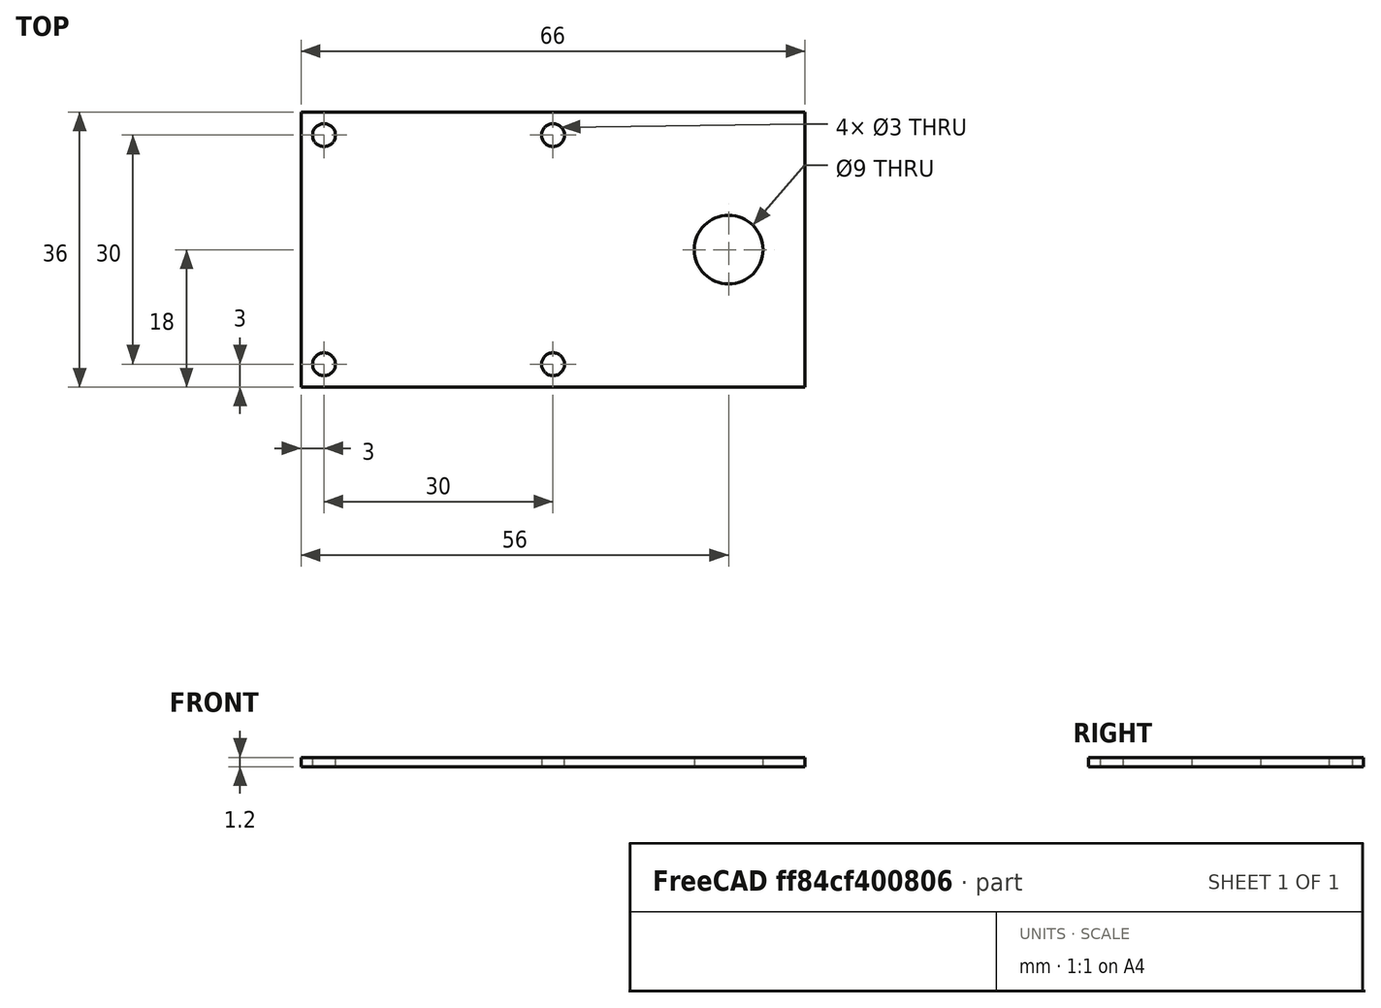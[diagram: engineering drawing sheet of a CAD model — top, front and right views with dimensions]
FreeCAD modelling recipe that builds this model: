
FCSTD DOCUMENT  (FreeCAD 0.16R6712 (Git))
Label: LCM PCB1
License: All rights reserved
LicenseURL: http://en.wikipedia.org/wiki/All_rights_reserved
objects: Sketcher::SketchObject×1, PartDesign::Pad×1
note: 3 computed .brp shape members not serialized (recipe doc carries the construction recipe); baked Part::Feature solids carry a one-line shape summary decoded from their .brp

FEATURE [Sketcher::SketchObject] Sketch
  sketch-geometry (9):
    g0: LineSegment StartX=0 StartY=0 StartZ=0 EndX=66 EndY=0 EndZ=0
    g1: LineSegment StartX=66 StartY=0 StartZ=0 EndX=66 EndY=-36 EndZ=0
    g2: LineSegment StartX=66 StartY=-36 StartZ=0 EndX=0 EndY=-36 EndZ=0
    g3: LineSegment StartX=0 StartY=-36 StartZ=0 EndX=0 EndY=0 EndZ=0
    g4: Circle CenterX=3 CenterY=-3 CenterZ=0 NormalX=0 NormalY=0 NormalZ=1 Radius=1.5
    g5: Circle CenterX=33 CenterY=-3 CenterZ=0 NormalX=0 NormalY=0 NormalZ=1 Radius=1.5
    g6: Circle CenterX=3 CenterY=-33 CenterZ=0 NormalX=0 NormalY=0 NormalZ=1 Radius=1.5
    g7: Circle CenterX=33 CenterY=-33 CenterZ=0 NormalX=0 NormalY=0 NormalZ=1 Radius=1.5
    g8: Circle CenterX=56 CenterY=-18 CenterZ=0 NormalX=0 NormalY=0 NormalZ=1 Radius=4.5
  constraints (26):
    c: Coincident(g0,g1)
    c: Coincident(g1,g2)
    c: Coincident(g2,g3)
    c: Coincident(g3,g0)
    c: Horizontal(g0)
    c: Horizontal(g2)
    c: Vertical(g1)
    c: Vertical(g3)
    c: Coincident(g0,g-1)
    c: DistanceY(g3,g3) = 36
    c: DistanceX(g0,g0) = 66
    c: Radius(g4) = 1.5
    c: Equal(g4,g5)
    c: Equal(g4,g6)
    c: Equal(g4,g7)
    c: DistanceY(g5,g4) = 0
    c: DistanceY(g7,g6) = 0
    c: DistanceX(g4,g6) = 0
    c: DistanceX(g5,g7) = 0
    c: DistanceX(g-1,g4) = 3
    c: DistanceY(g4,g-1) = 3
    c: DistanceY(g2,g6) = 3
    c: DistanceX(g6,g7) = 30
    c: Radius(g8) = 4.5
    c: DistanceX(g8,g0) = 10
    c: DistanceY(g8,g0) = 18
FEATURE [PartDesign::Pad] Pad
  Length = 1.2
  Length2 = 100
  Sketch = -> Sketch
  Type = 0
